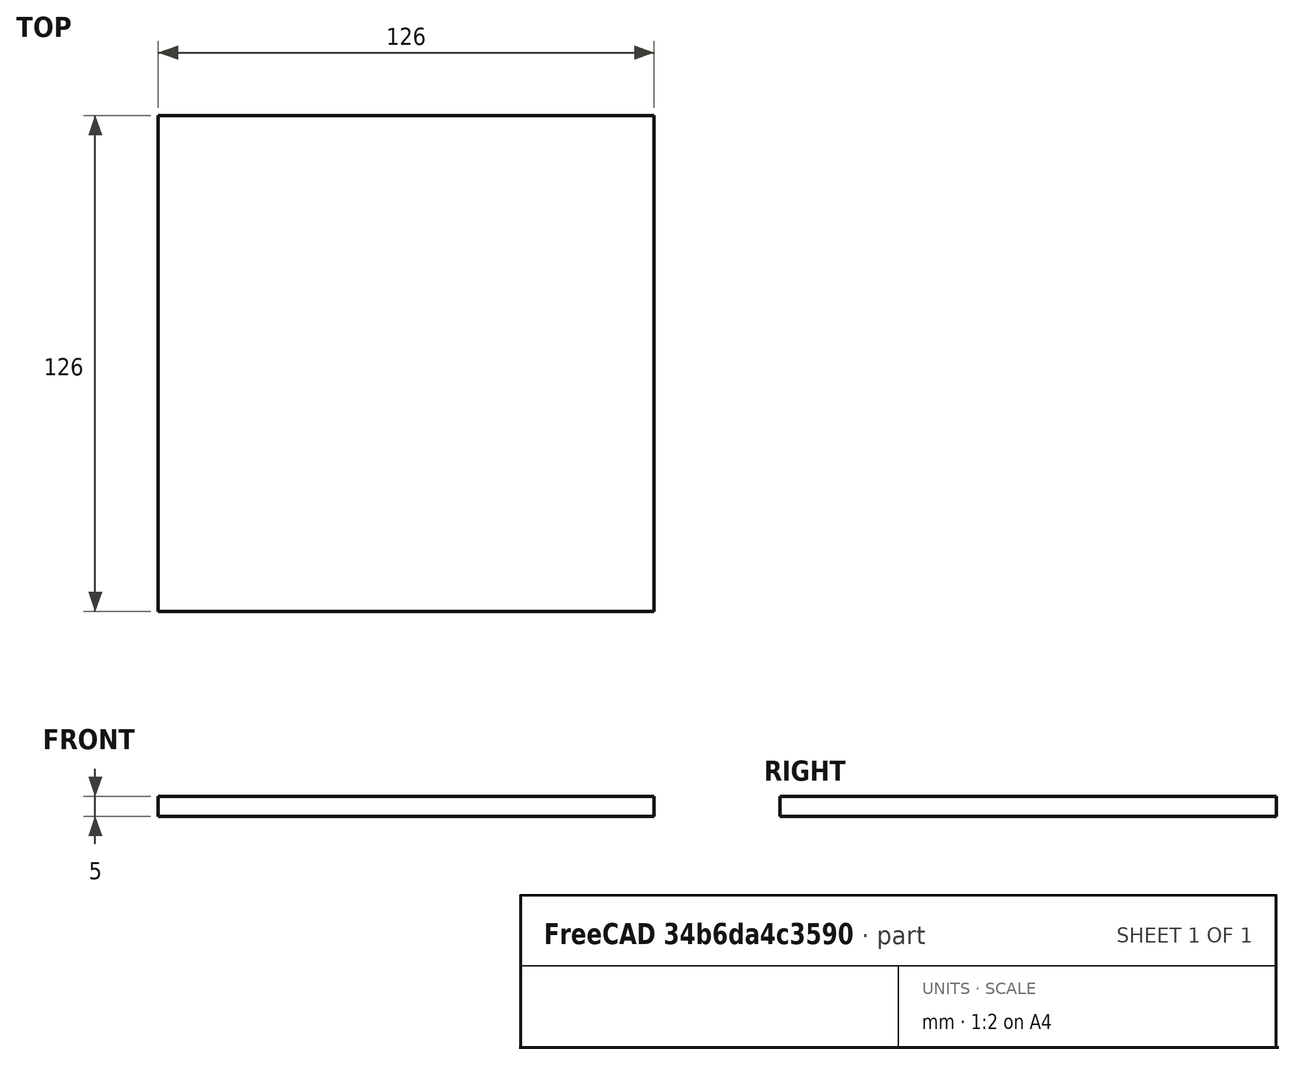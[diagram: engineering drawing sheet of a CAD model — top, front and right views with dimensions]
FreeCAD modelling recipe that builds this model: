
FCSTD DOCUMENT  (FreeCAD 1.0R39319 (Git))
Label: semantic
License: All rights reserved
LicenseURL: https://en.wikipedia.org/wiki/All_rights_reserved
objects: Sketcher::SketchObject×1, PartDesign::Pad×1, PartDesign::Body×1
note: 6 computed .brp shape members not serialized (recipe doc carries the construction recipe); baked Part::Feature solids carry a one-line shape summary decoded from their .brp

FEATURE [Sketcher::SketchObject] Sketch_1
  ArcFitTolerance = 1e-06
  AttachmentSupport = -> [XY_Plane]
  FullyConstrained = false
  MakeInternals = false
  MapMode = 5
  sketch-geometry (4):
    g0: LineSegment StartX=-63 StartY=-63 StartZ=0 EndX=63 EndY=-63 EndZ=0
    g1: LineSegment StartX=63 StartY=-63 StartZ=0 EndX=63 EndY=63 EndZ=0
    g2: LineSegment StartX=63 StartY=63 StartZ=0 EndX=-63 EndY=63 EndZ=0
    g3: LineSegment StartX=-63 StartY=63 StartZ=0 EndX=-63 EndY=-63 EndZ=0
  constraints (4):
    c: Coincident(g0,g1)
    c: Coincident(g1,g2)
    c: Coincident(g2,g3)
    c: Coincident(g3,g0)
FEATURE [PartDesign::Pad] Pad_1
  Direction = (0,0,1)
  Length = 5
  Length2 = 10
  Profile = -> Sketch_1
  Refine = true
  Suppressed = false
  Type = 0
FEATURE [PartDesign::Body] Body
  AllowCompound = false
  Group = -> [Sketch_1,Pad_1]
  Origin = -> Origin
  Tip = -> Pad_1
